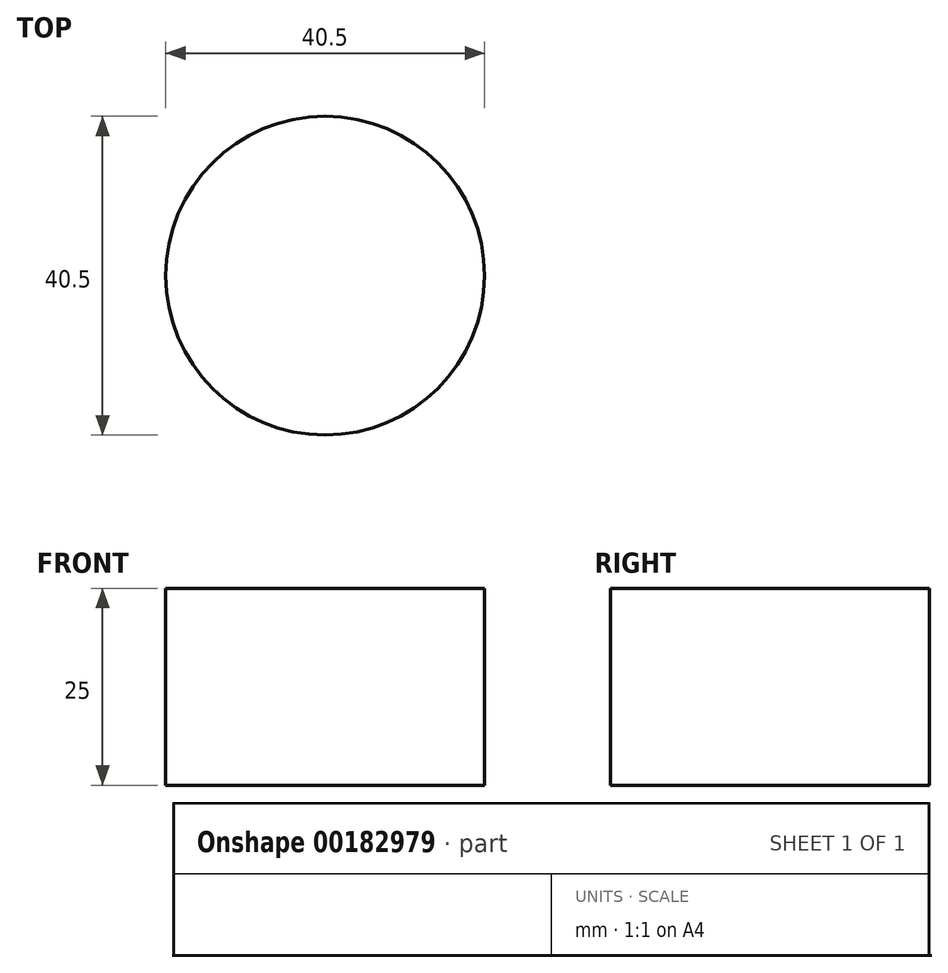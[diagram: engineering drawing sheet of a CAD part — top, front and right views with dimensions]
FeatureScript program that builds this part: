
annotation { "Feature Type Name" : "Feature", "Feature Type Description" : "" }
export const myFeature = defineFeature(function(context is Context, id is Id, definition is map)
    precondition{}
    {
        {
            var Q0;
            Q0=qCreatedBy(makeId("Top.planeOp"),FACE);
            var sketch = newSketch(context, id + "F0", { "sketchPlane" : qUnion([Q0])});
            skCircle(sketch, "E0", {"center": v(0, 0) * mm, "radius": 20.25 * mm});
            skCircle(sketch, "E1", {"center": v(0, 0) * mm, "radius": 21.45 * mm});
            skLineSegment(sketch, "E2", {"start": v(0, 0) * mm, "end": v(51.08, -52.48) * mm, "construction": true});
            skLineSegment(sketch, "E3", {"start": v(43.68, 42.1) * mm, "end": v(-48.51, -46.76) * mm, "construction": true});
            skCircle(sketch, "E4", {"center": v(11.82, -12.15) * mm, "radius": 3 * mm});
            skCircle(sketch, "E5", {"center": v(11.82, -12.15) * mm, "radius": 4.5 * mm});
            skSolve(sketch);
        }
        {
            var Q0;
            {var subQ0=sQuery(id+"F0.wireOp",EDGE,"E5");var subQ1=sQuery(id+"F0.wireOp",EDGE,"E0");var subQ2=makeQuery(id+"F0.imprint","INTERSECT",VERTEX,{"disambiguationData":[OD(0.0)],"derivedFrom":[subQ1,subQ0]});Q0=makeQuery(id+"F0.imprint","IMPRINT",FACE,{"disambiguationData":[TD([[makeQuery(id+"F0.imprint","IMPRINT",EDGE,{"disambiguationData":[TD([[subQ2,1.0]])],"derivedFrom":subQ1}),1.0]])]});}
            var Q1;
            Q1=makeQuery(id+"F0.imprint","IMPRINT",FACE,{"disambiguationData":[TD([[makeQuery(id+"F0.imprint","IMPRINT",EDGE,{"derivedFrom":sQuery(id+"F0.wireOp",EDGE,"E4")}),-1.0]])]});
            var Q2;
            Q2=makeQuery(id+"F0.imprint","IMPRINT",FACE,{"disambiguationData":[TD([[makeQuery(id+"F0.imprint","IMPRINT",EDGE,{"derivedFrom":sQuery(id+"F0.wireOp",EDGE,"E4")}),1.0]])]});
            extrude(context, id + "F1", {"entities" : qUnion([Q0, Q1, Q2]), "depth" : 25 * mm});
        }
    });
